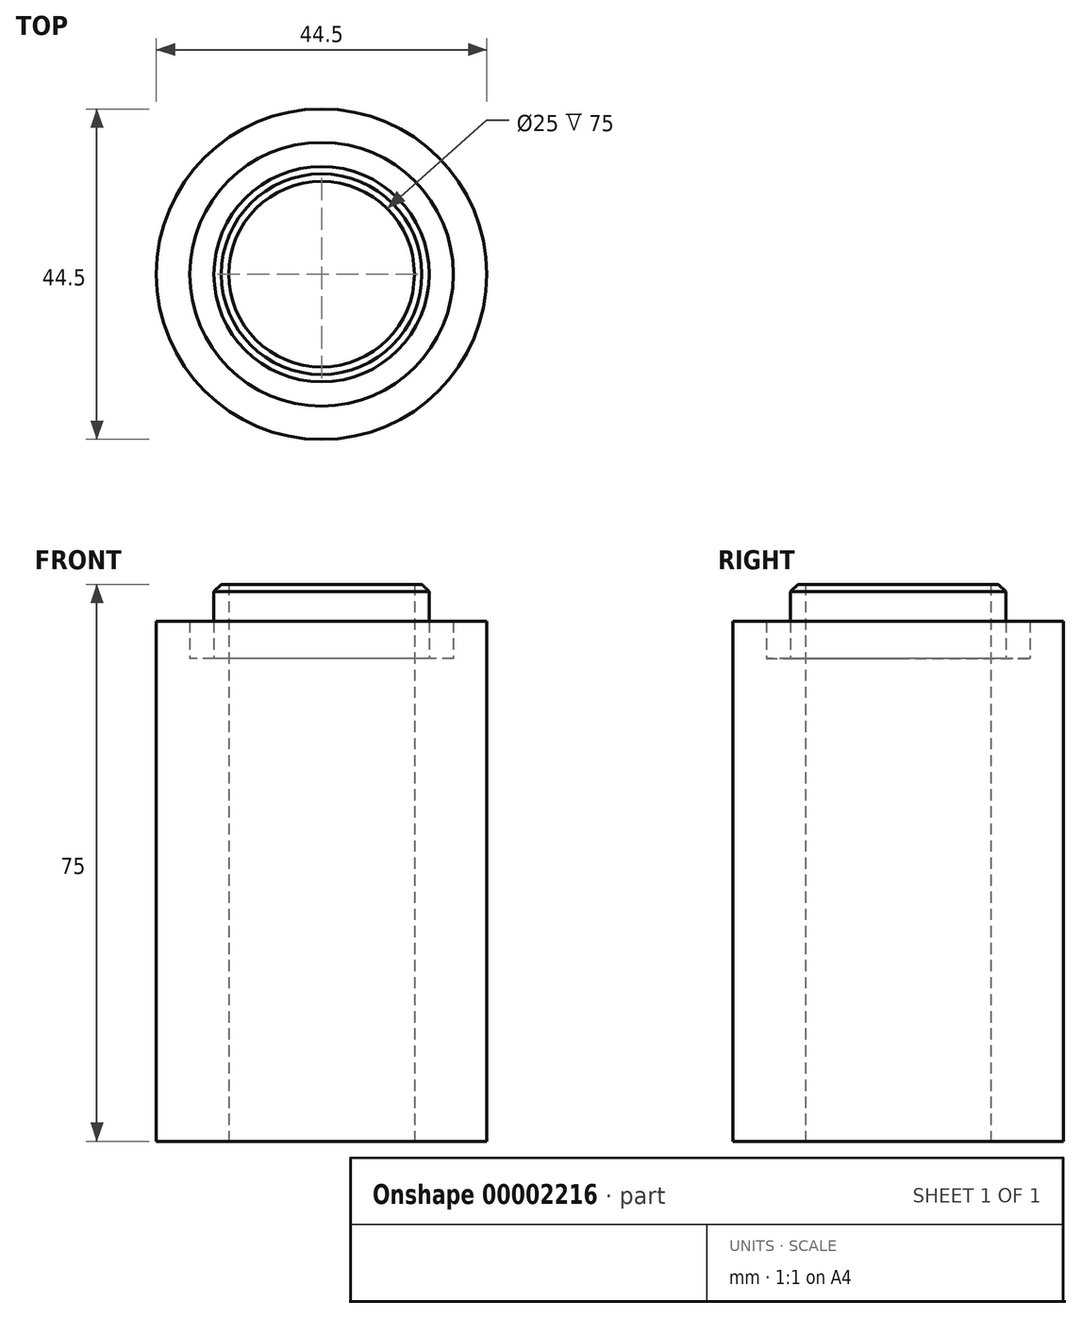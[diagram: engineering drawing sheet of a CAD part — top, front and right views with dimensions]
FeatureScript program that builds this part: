
annotation { "Feature Type Name" : "Feature", "Feature Type Description" : "" }
export const myFeature = defineFeature(function(context is Context, id is Id, definition is map)
    precondition{}
    {
        {
            var Q0;
            Q0=qCreatedBy(makeId("Top.planeOp"),FACE);
            var sketch = newSketch(context, id + "F0", { "sketchPlane" : qUnion([Q0])});
            skCircle(sketch, "E0", {"center": v(0, 0) * mm, "radius": 22.25 * mm});
            skCircle(sketch, "E1", {"center": v(0, 0) * mm, "radius": 17.75 * mm});
            skCircle(sketch, "E2", {"center": v(0, 0) * mm, "radius": 14.5 * mm});
            skCircle(sketch, "E3", {"center": v(0, 0) * mm, "radius": 12.5 * mm});
            skSolve(sketch);
        }
        {
            var Q0;
            Q0=makeQuery(id+"F0.imprint","IMPRINT",FACE,{"disambiguationData":[TD([[makeQuery(id+"F0.imprint","IMPRINT",EDGE,{"derivedFrom":sQuery(id+"F0.wireOp",EDGE,"E0")}),1.0]])]});
            extrude(context, id + "F1", {"entities" : qUnion([Q0]), "depth" : 70 * mm});
        }
        {
            var Q0;
            Q0=makeQuery(id+"F0.imprint","IMPRINT",FACE,{"disambiguationData":[TD([[makeQuery(id+"F0.imprint","IMPRINT",EDGE,{"derivedFrom":sQuery(id+"F0.wireOp",EDGE,"E1")}),1.0]])]});
            extrude(context, id + "F2", {"entities" : qUnion([Q0]), "operationType" : NewBodyOperationType.ADD, "depth" : 65 * mm});
        }
        {
            var Q0;
            Q0=makeQuery(id+"F0.imprint","IMPRINT",FACE,{"disambiguationData":[TD([[makeQuery(id+"F0.imprint","IMPRINT",EDGE,{"derivedFrom":sQuery(id+"F0.wireOp",EDGE,"E2")}),1.0]])]});
            extrude(context, id + "F3", {"entities" : qUnion([Q0]), "operationType" : NewBodyOperationType.ADD, "depth" : 75 * mm});
        }
        {
            var Q0;
            Q0=makeQuery(id+"F3.opExtrude","CAP_EDGE",EDGE,{"disambiguationData":[OSD([sQuery(id+"F0.wireOp",EDGE,"E2")])],"isStart":false});
            chamfer(context, id + "F4", {"entities" : qUnion([Q0]), "width" : 1 * mm, "tangentPropagation" : true});
        }
    });
